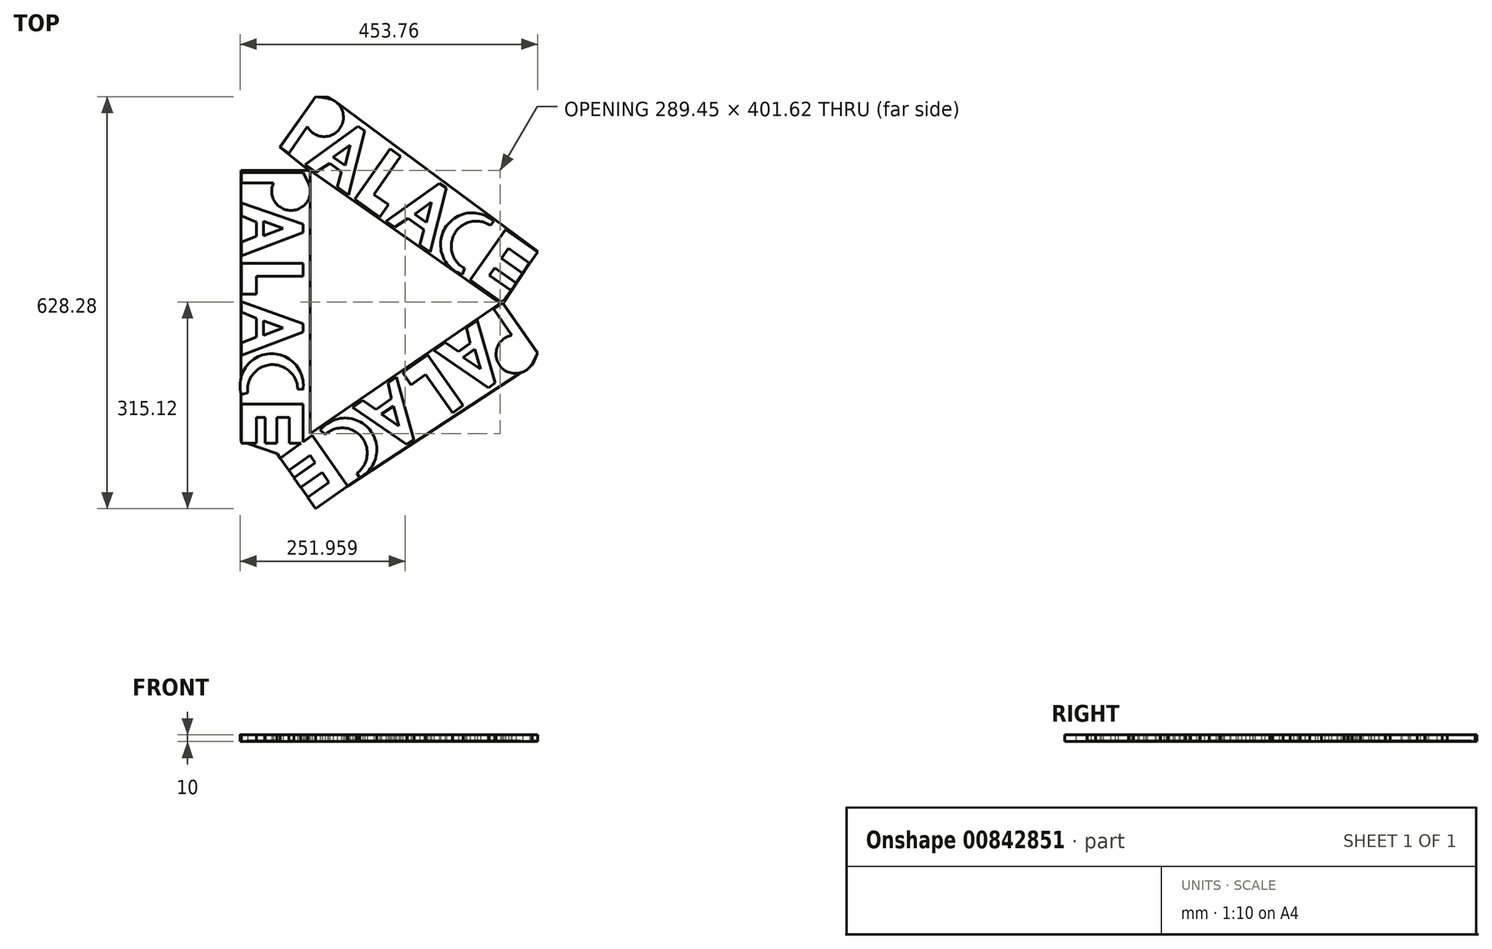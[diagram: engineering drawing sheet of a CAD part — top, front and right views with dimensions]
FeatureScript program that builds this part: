
annotation { "Feature Type Name" : "Feature", "Feature Type Description" : "" }
export const myFeature = defineFeature(function(context is Context, id is Id, definition is map)
    precondition{}
    {
        {
            var Q0;
            Q0=qCreatedBy(makeId("Top.planeOp"),FACE);
            var sketch = newSketch(context, id + "F0", { "sketchPlane" : qUnion([Q0])});
            skLineSegment(sketch, "E0", {"start": v(-235.7, 282.24) * mm, "end": v(-329.78, 282.24) * mm});
            skLineSegment(sketch, "E1", {"start": v(-329.78, 282.24) * mm, "end": v(-329.78, 265.88) * mm});
            skLineSegment(sketch, "E2", {"start": v(-329.78, 265.88) * mm, "end": v(-280.65, 265.88) * mm});
            skLineSegment(sketch, "E3", {"start": v(-329.78, 235.57) * mm, "end": v(-235.7, 203.16) * mm});
            skLineSegment(sketch, "E4", {"start": v(-235.7, 203.16) * mm, "end": v(-235.7, 190.61) * mm});
            skLineSegment(sketch, "E5", {"start": v(-235.7, 190.61) * mm, "end": v(-329.78, 155.07) * mm});
            skLineSegment(sketch, "E6", {"start": v(-329.78, 155.07) * mm, "end": v(-329.78, 175.98) * mm});
            skLineSegment(sketch, "E7", {"start": v(-329.78, 175.98) * mm, "end": v(-307.02, 184.58) * mm});
            skLineSegment(sketch, "E8", {"start": v(-307.02, 184.58) * mm, "end": v(-307.02, 206.3) * mm});
            skLineSegment(sketch, "E9", {"start": v(-307.02, 206.3) * mm, "end": v(-329.78, 215.7) * mm});
            skLineSegment(sketch, "E10", {"start": v(-329.78, 215.7) * mm, "end": v(-329.78, 235.57) * mm});
            skLineSegment(sketch, "E11", {"start": v(-235.7, 143.57) * mm, "end": v(-329.78, 143.57) * mm});
            skLineSegment(sketch, "E12", {"start": v(-329.78, 143.57) * mm, "end": v(-329.78, 96.53) * mm});
            skLineSegment(sketch, "E13", {"start": v(-329.78, 96.53) * mm, "end": v(-307.02, 96.53) * mm});
            skLineSegment(sketch, "E14", {"start": v(-307.02, 96.53) * mm, "end": v(-307.02, 123.7) * mm});
            skLineSegment(sketch, "E15", {"start": v(-307.02, 123.7) * mm, "end": v(-235.7, 123.7) * mm});
            skLineSegment(sketch, "E16", {"start": v(-235.7, 123.7) * mm, "end": v(-235.7, 143.57) * mm});
            skLineSegment(sketch, "E17", {"start": v(-329.78, 85.03) * mm, "end": v(-235.7, 51.57) * mm});
            skLineSegment(sketch, "E18", {"start": v(-235.7, 51.57) * mm, "end": v(-235.7, 39.03) * mm});
            skLineSegment(sketch, "E19", {"start": v(-235.7, 39.03) * mm, "end": v(-329.78, 3.49) * mm});
            skLineSegment(sketch, "E20", {"start": v(-329.78, 3.49) * mm, "end": v(-329.78, 22.3) * mm});
            skLineSegment(sketch, "E21", {"start": v(-329.78, 22.3) * mm, "end": v(-307.02, 30.9) * mm});
            skLineSegment(sketch, "E22", {"start": v(-307.02, 30.9) * mm, "end": v(-307.02, 59.97) * mm});
            skLineSegment(sketch, "E23", {"start": v(-307.02, 59.97) * mm, "end": v(-329.78, 69.38) * mm});
            skLineSegment(sketch, "E24", {"start": v(-329.78, 69.38) * mm, "end": v(-329.78, 85.03) * mm});
            skLineSegment(sketch, "E25", {"start": v(-329.78, -71.04) * mm, "end": v(-329.78, -131.08) * mm});
            skLineSegment(sketch, "E26", {"start": v(-329.78, -131.08) * mm, "end": v(-307.02, -131.08) * mm});
            skLineSegment(sketch, "E27", {"start": v(-307.02, -131.08) * mm, "end": v(-307.02, -91.23) * mm});
            skLineSegment(sketch, "E28", {"start": v(-307.02, -91.23) * mm, "end": v(-293.4, -91.23) * mm});
            skLineSegment(sketch, "E29", {"start": v(-293.4, -91.23) * mm, "end": v(-293.4, -131.08) * mm});
            skLineSegment(sketch, "E30", {"start": v(-293.4, -131.08) * mm, "end": v(-275.39, -131.08) * mm});
            skLineSegment(sketch, "E31", {"start": v(-275.39, -131.08) * mm, "end": v(-275.39, -91.23) * mm});
            skLineSegment(sketch, "E32", {"start": v(-275.39, -91.23) * mm, "end": v(-256.83, -91.23) * mm});
            skLineSegment(sketch, "E33", {"start": v(-256.83, -91.23) * mm, "end": v(-256.83, -131.08) * mm});
            skLineSegment(sketch, "E34", {"start": v(-256.83, -131.08) * mm, "end": v(-235.7, -131.08) * mm});
            skLineSegment(sketch, "E35", {"start": v(-235.7, -131.08) * mm, "end": v(-235.7, -71.04) * mm});
            skLineSegment(sketch, "E36", {"start": v(-235.7, -71.04) * mm, "end": v(-329.78, -71.04) * mm});
            skArc(sketch, "E37", {"start": v(-280.65, 265.88) * mm, "mid": v(-254, 224.07) * mm, "end": v(-227.35, 265.88) * mm});
            skLineSegment(sketch, "E38", {"start": v(-227.35, 265.88) * mm, "end": v(-235.7, 282.24) * mm});
            skArc(sketch, "E39", {"start": v(-235.7, -49.2) * mm, "mid": v(-287.14, 5.5) * mm, "end": v(-329.78, -56.3) * mm});
            skArc(sketch, "E40", {"start": v(-243.73, -48.46) * mm, "mid": v(-284.93, -11.12) * mm, "end": v(-320, -54.26) * mm});
            skLineSegment(sketch, "E41", {"start": v(-243.73, -48.46) * mm, "end": v(-235.7, -49.2) * mm});
            skLineSegment(sketch, "E42", {"start": v(-320, -54.26) * mm, "end": v(-329.78, -56.3) * mm});
            skPoint(sketch, "E43.startSnap0", {"position": v(-282.74, 68.3) * mm});
            skLineSegment(sketch, "E44", {"start": v(-295.92, 55.92) * mm, "end": v(-295.92, 33.9) * mm});
            skLineSegment(sketch, "E45", {"start": v(-295.92, 33.9) * mm, "end": v(-265.9, 45.24) * mm});
            skLineSegment(sketch, "E46", {"start": v(-265.9, 45.24) * mm, "end": v(-295.92, 55.92) * mm});
            skLineSegment(sketch, "E47", {"start": v(-295.84, 207.46) * mm, "end": v(-295.84, 185.44) * mm});
            skLineSegment(sketch, "E48", {"start": v(-295.84, 185.44) * mm, "end": v(-265.81, 196.78) * mm});
            skLineSegment(sketch, "E49", {"start": v(-265.81, 196.78) * mm, "end": v(-295.84, 207.46) * mm});
            skLineSegment(sketch, "E50", {"start": v(122, 6.5) * mm, "end": v(69.17, 81.95) * mm});
            skLineSegment(sketch, "E51", {"start": v(67.01, 82.87) * mm, "end": v(54.63, 74.2) * mm});
            skLineSegment(sketch, "E52", {"start": v(54.63, 74.2) * mm, "end": v(82.81, 33.95) * mm});
            skLineSegment(sketch, "E53", {"start": v(29.8, 56.8) * mm, "end": v(57.22, -38.85) * mm});
            skLineSegment(sketch, "E54", {"start": v(57.22, -38.85) * mm, "end": v(46.94, -46.04) * mm});
            skLineSegment(sketch, "E55", {"start": v(46.94, -46.04) * mm, "end": v(-36.14, 10.64) * mm});
            skLineSegment(sketch, "E56", {"start": v(-36.14, 10.64) * mm, "end": v(-19.01, 22.63) * mm});
            skLineSegment(sketch, "E57", {"start": v(-19.01, 22.63) * mm, "end": v(1.1, 8.91) * mm});
            skLineSegment(sketch, "E58", {"start": v(1.1, 8.91) * mm, "end": v(18.88, 21.37) * mm});
            skLineSegment(sketch, "E59", {"start": v(18.88, 21.37) * mm, "end": v(13.53, 45.42) * mm});
            skLineSegment(sketch, "E60", {"start": v(13.53, 45.42) * mm, "end": v(29.8, 56.8) * mm});
            skLineSegment(sketch, "E61", {"start": v(8.4, -73.03) * mm, "end": v(-45.56, 4.04) * mm});
            skLineSegment(sketch, "E62", {"start": v(-45.56, 4.04) * mm, "end": v(-84.1, -22.94) * mm});
            skLineSegment(sketch, "E63", {"start": v(-84.1, -22.94) * mm, "end": v(-71.04, -41.6) * mm});
            skLineSegment(sketch, "E64", {"start": v(-71.04, -41.6) * mm, "end": v(-48.77, -26) * mm});
            skLineSegment(sketch, "E65", {"start": v(-48.77, -26) * mm, "end": v(-7.87, -84.42) * mm});
            skLineSegment(sketch, "E66", {"start": v(-7.87, -84.42) * mm, "end": v(8.4, -73.03) * mm});
            skLineSegment(sketch, "E67", {"start": v(-93.52, -29.54) * mm, "end": v(-66.95, -125.8) * mm});
            skLineSegment(sketch, "E68", {"start": v(-66.95, -125.8) * mm, "end": v(-77.23, -132.99) * mm});
            skLineSegment(sketch, "E69", {"start": v(-77.23, -132.99) * mm, "end": v(-160.31, -76.3) * mm});
            skLineSegment(sketch, "E70", {"start": v(-160.31, -76.3) * mm, "end": v(-144.9, -65.51) * mm});
            skLineSegment(sketch, "E71", {"start": v(-144.9, -65.51) * mm, "end": v(-124.8, -79.23) * mm});
            skLineSegment(sketch, "E72", {"start": v(-124.8, -79.23) * mm, "end": v(-100.98, -62.56) * mm});
            skLineSegment(sketch, "E73", {"start": v(-100.98, -62.56) * mm, "end": v(-106.34, -38.51) * mm});
            skLineSegment(sketch, "E74", {"start": v(-106.34, -38.51) * mm, "end": v(-93.52, -29.54) * mm});
            skLineSegment(sketch, "E75", {"start": v(-221.36, -119.05) * mm, "end": v(-270.54, -153.49) * mm});
            skLineSegment(sketch, "E76", {"start": v(-270.54, -153.49) * mm, "end": v(-257.48, -172.14) * mm});
            skLineSegment(sketch, "E77", {"start": v(-257.48, -172.14) * mm, "end": v(-224.84, -149.29) * mm});
            skLineSegment(sketch, "E78", {"start": v(-224.84, -149.29) * mm, "end": v(-217.03, -160.44) * mm});
            skLineSegment(sketch, "E79", {"start": v(-217.03, -160.44) * mm, "end": v(-249.67, -183.3) * mm});
            skLineSegment(sketch, "E80", {"start": v(-249.67, -183.3) * mm, "end": v(-239.34, -198.05) * mm});
            skLineSegment(sketch, "E81", {"start": v(-239.34, -198.05) * mm, "end": v(-206.7, -175.2) * mm});
            skLineSegment(sketch, "E82", {"start": v(-206.7, -175.2) * mm, "end": v(-196.05, -190.4) * mm});
            skLineSegment(sketch, "E83", {"start": v(-196.05, -190.4) * mm, "end": v(-228.7, -213.25) * mm});
            skLineSegment(sketch, "E84", {"start": v(-228.7, -213.25) * mm, "end": v(-216.57, -230.56) * mm});
            skLineSegment(sketch, "E85", {"start": v(-216.57, -230.56) * mm, "end": v(-167.4, -196.12) * mm});
            skLineSegment(sketch, "E86", {"start": v(-167.4, -196.12) * mm, "end": v(-221.36, -119.05) * mm});
            skArc(sketch, "E87", {"start": v(82.81, 33.95) * mm, "mid": v(63.85, -11.86) * mm, "end": v(113.39, -9.7) * mm});
            skLineSegment(sketch, "E88", {"start": v(113.39, -9.7) * mm, "end": v(122, 6.5) * mm});
            skArc(sketch, "E89", {"start": v(-149.5, -183.6) * mm, "mid": v(-134.2, -110.08) * mm, "end": v(-209.28, -110.6) * mm});
            skArc(sketch, "E90", {"start": v(-153.5, -176.6) * mm, "mid": v(-146.55, -121.43) * mm, "end": v(-202, -117.44) * mm});
            skLineSegment(sketch, "E91", {"start": v(-153.5, -176.6) * mm, "end": v(-149.5, -183.6) * mm});
            skLineSegment(sketch, "E92", {"start": v(-202, -117.44) * mm, "end": v(-209.28, -110.6) * mm});
            skPoint(sketch, "E93.startSnap0", {"position": v(-80.23, -77.66) * mm});
            skLineSegment(sketch, "E94", {"start": v(-97.93, -73.98) * mm, "end": v(-115.97, -86.6) * mm});
            skLineSegment(sketch, "E95", {"start": v(-115.97, -86.6) * mm, "end": v(-89.46, -104.7) * mm});
            skLineSegment(sketch, "E96", {"start": v(-89.46, -104.7) * mm, "end": v(-97.93, -73.98) * mm});
            skLineSegment(sketch, "E97", {"start": v(26.25, 12.88) * mm, "end": v(8.2, 0.25) * mm});
            skLineSegment(sketch, "E98", {"start": v(8.2, 0.25) * mm, "end": v(34.72, -17.84) * mm});
            skLineSegment(sketch, "E99", {"start": v(34.72, -17.84) * mm, "end": v(26.25, 12.88) * mm});
            skLineSegment(sketch, "E100.0", {"start": v(82.81, 33.95) * mm, "end": v(113.39, -9.7) * mm, "construction": true});
            skLineSegment(sketch, "E101.0", {"start": v(-270.54, -153.49) * mm, "end": v(-228.7, -213.25) * mm, "construction": true});
            skLineSegment(sketch, "E102.0", {"start": v(-221.36, -119.05) * mm, "end": v(-167.4, -196.12) * mm, "construction": true});
            skLineSegment(sketch, "E103.0", {"start": v(-217.03, -160.44) * mm, "end": v(-206.7, -175.2) * mm, "construction": true});
            skLineSegment(sketch, "E104.0", {"start": v(-221.36, -119.05) * mm, "end": v(67.01, 82.87) * mm, "construction": true});
            skLineSegment(sketch, "E105.0", {"start": v(-167.4, -196.12) * mm, "end": v(-77.23, -132.99) * mm, "construction": true});
            skLineSegment(sketch, "E106.0", {"start": v(-257.48, -172.14) * mm, "end": v(1.1, 8.91) * mm, "construction": true});
            skLineSegment(sketch, "E107.0", {"start": v(-7.87, -84.42) * mm, "end": v(122, 6.5) * mm, "construction": true});
            skLineSegment(sketch, "E108.0", {"start": v(29.8, 56.8) * mm, "end": v(54.63, 74.2) * mm, "construction": true});
            skLineSegment(sketch, "E109.0", {"start": v(-66.95, -125.8) * mm, "end": v(8.4, -73.03) * mm, "construction": true});
            skLineSegment(sketch, "E110", {"start": v(-216.57, 397.72) * mm, "end": v(-270.54, 320.65) * mm});
            skLineSegment(sketch, "E111", {"start": v(-270.54, 320.65) * mm, "end": v(-257.14, 311.27) * mm});
            skLineSegment(sketch, "E112", {"start": v(-257.14, 311.27) * mm, "end": v(-228.96, 351.52) * mm});
            skLineSegment(sketch, "E113", {"start": v(-232.3, 293.88) * mm, "end": v(-151.8, 352.36) * mm});
            skLineSegment(sketch, "E114", {"start": v(-151.8, 352.36) * mm, "end": v(-141.52, 345.17) * mm});
            skLineSegment(sketch, "E115", {"start": v(-141.52, 345.17) * mm, "end": v(-166.37, 247.7) * mm});
            skLineSegment(sketch, "E116", {"start": v(-166.37, 247.7) * mm, "end": v(-183.5, 259.7) * mm});
            skLineSegment(sketch, "E117", {"start": v(-183.5, 259.7) * mm, "end": v(-177.48, 283.29) * mm});
            skLineSegment(sketch, "E118", {"start": v(-177.48, 283.29) * mm, "end": v(-195.27, 295.74) * mm});
            skLineSegment(sketch, "E119", {"start": v(-195.27, 295.74) * mm, "end": v(-216.04, 282.49) * mm});
            skLineSegment(sketch, "E120", {"start": v(-216.04, 282.49) * mm, "end": v(-232.3, 293.88) * mm});
            skLineSegment(sketch, "E121", {"start": v(-102.98, 318.18) * mm, "end": v(-156.95, 241.11) * mm});
            skLineSegment(sketch, "E122", {"start": v(-156.95, 241.11) * mm, "end": v(-118.41, 214.13) * mm});
            skLineSegment(sketch, "E123", {"start": v(-118.41, 214.13) * mm, "end": v(-105.35, 232.78) * mm});
            skLineSegment(sketch, "E124", {"start": v(-105.35, 232.78) * mm, "end": v(-127.62, 248.37) * mm});
            skLineSegment(sketch, "E125", {"start": v(-127.62, 248.37) * mm, "end": v(-86.71, 306.8) * mm});
            skLineSegment(sketch, "E126", {"start": v(-86.71, 306.8) * mm, "end": v(-102.98, 318.18) * mm});
            skLineSegment(sketch, "E127", {"start": v(-109, 207.53) * mm, "end": v(-27.63, 265.42) * mm});
            skLineSegment(sketch, "E128", {"start": v(-27.63, 265.42) * mm, "end": v(-17.35, 258.22) * mm});
            skLineSegment(sketch, "E129", {"start": v(-17.35, 258.22) * mm, "end": v(-42.2, 160.76) * mm});
            skLineSegment(sketch, "E130", {"start": v(-42.2, 160.76) * mm, "end": v(-57.61, 171.56) * mm});
            skLineSegment(sketch, "E131", {"start": v(-57.61, 171.56) * mm, "end": v(-51.6, 195.14) * mm});
            skLineSegment(sketch, "E132", {"start": v(-51.6, 195.14) * mm, "end": v(-75.4, 211.81) * mm});
            skLineSegment(sketch, "E133", {"start": v(-75.4, 211.81) * mm, "end": v(-96.17, 198.56) * mm});
            skLineSegment(sketch, "E134", {"start": v(-96.17, 198.56) * mm, "end": v(-109, 207.53) * mm});
            skLineSegment(sketch, "E135", {"start": v(18.85, 118.02) * mm, "end": v(65.66, 85.24) * mm});
            skLineSegment(sketch, "E136", {"start": v(70, 86.4) * mm, "end": v(81.09, 102.23) * mm});
            skLineSegment(sketch, "E137", {"start": v(81.09, 102.23) * mm, "end": v(48.45, 125.09) * mm});
            skLineSegment(sketch, "E138", {"start": v(48.45, 125.09) * mm, "end": v(56.26, 136.24) * mm});
            skLineSegment(sketch, "E139", {"start": v(56.26, 136.24) * mm, "end": v(88.9, 113.39) * mm});
            skLineSegment(sketch, "E140", {"start": v(88.9, 113.39) * mm, "end": v(99.23, 128.14) * mm});
            skLineSegment(sketch, "E141", {"start": v(99.23, 128.14) * mm, "end": v(66.6, 151) * mm});
            skLineSegment(sketch, "E142", {"start": v(66.6, 151) * mm, "end": v(77.24, 166.2) * mm});
            skLineSegment(sketch, "E143", {"start": v(77.24, 166.2) * mm, "end": v(109.88, 143.34) * mm});
            skLineSegment(sketch, "E144", {"start": v(109.88, 143.34) * mm, "end": v(122, 160.65) * mm});
            skLineSegment(sketch, "E145", {"start": v(122, 160.65) * mm, "end": v(72.81, 195.1) * mm});
            skLineSegment(sketch, "E146", {"start": v(72.81, 195.1) * mm, "end": v(18.85, 118.02) * mm});
            skArc(sketch, "E147", {"start": v(-228.96, 351.52) * mm, "mid": v(-179.42, 349.36) * mm, "end": v(-198.39, 395.18) * mm});
            skLineSegment(sketch, "E148", {"start": v(-198.39, 395.18) * mm, "end": v(-216.57, 397.72) * mm});
            skArc(sketch, "E149", {"start": v(54.93, 207.61) * mm, "mid": v(-19.39, 196.86) * mm, "end": v(6.77, 126.47) * mm});
            skArc(sketch, "E150", {"start": v(49.7, 201.46) * mm, "mid": v(-4.5, 189.13) * mm, "end": v(10.72, 135.65) * mm});
            skLineSegment(sketch, "E151", {"start": v(49.7, 201.46) * mm, "end": v(54.93, 207.61) * mm});
            skLineSegment(sketch, "E152", {"start": v(10.72, 135.65) * mm, "end": v(6.77, 126.47) * mm});
            skPoint(sketch, "E153.startSnap0", {"position": v(-68.3, 236.48) * mm});
            skLineSegment(sketch, "E154", {"start": v(-65.72, 218.58) * mm, "end": v(-47.69, 205.95) * mm});
            skLineSegment(sketch, "E155", {"start": v(-47.69, 205.95) * mm, "end": v(-39.76, 237.05) * mm});
            skLineSegment(sketch, "E156", {"start": v(-39.76, 237.05) * mm, "end": v(-65.72, 218.58) * mm});
            skLineSegment(sketch, "E157", {"start": v(-189.81, 305.57) * mm, "end": v(-171.78, 292.94) * mm});
            skLineSegment(sketch, "E158", {"start": v(-171.78, 292.94) * mm, "end": v(-163.84, 324.04) * mm});
            skLineSegment(sketch, "E159", {"start": v(-163.84, 324.04) * mm, "end": v(-189.81, 305.57) * mm});
            skLineSegment(sketch, "E160.0", {"start": v(-228.96, 351.52) * mm, "end": v(-198.39, 395.18) * mm, "construction": true});
            skLineSegment(sketch, "E161.0", {"start": v(70, 86.4) * mm, "end": v(109.88, 143.34) * mm, "construction": true});
            skLineSegment(sketch, "E162.0", {"start": v(18.85, 118.02) * mm, "end": v(72.81, 195.1) * mm, "construction": true});
            skLineSegment(sketch, "E163.0", {"start": v(56.26, 136.24) * mm, "end": v(66.6, 151) * mm, "construction": true});
            skLineSegment(sketch, "E164.0", {"start": v(72.81, 195.1) * mm, "end": v(-17.35, 258.22) * mm, "construction": true});
            skLineSegment(sketch, "E165.0", {"start": v(18.85, 118.02) * mm, "end": v(-270.54, 320.65) * mm, "construction": true});
            skLineSegment(sketch, "E166.0", {"start": v(81.09, 102.23) * mm, "end": v(-177.48, 283.29) * mm, "construction": true});
            skLineSegment(sketch, "E167.0", {"start": v(-232.3, 293.88) * mm, "end": v(-257.14, 311.27) * mm, "construction": true});
            skLineSegment(sketch, "E168.0", {"start": v(-86.71, 306.8) * mm, "end": v(-216.57, 397.72) * mm, "construction": true});
            skLineSegment(sketch, "E169.0", {"start": v(-27.63, 265.42) * mm, "end": v(-102.98, 318.18) * mm, "construction": true});
            skLineSegment(sketch, "E170", {"start": v(70, 86.4) * mm, "end": v(65.66, 85.24) * mm});
            skLineSegment(sketch, "E171", {"start": v(69.17, 81.95) * mm, "end": v(67.01, 82.87) * mm});
            skSolve(sketch);
        }
        {
            var Q0;
            Q0=qCreatedBy(makeId("Top.planeOp"),FACE);
            var sketch = newSketch(context, id + "F1", { "sketchPlane" : qUnion([Q0])});
            skLineSegment(sketch, "E172", {"start": v(-330.45, 285.37) * mm, "end": v(-330.45, -127.9) * mm});
            skLineSegment(sketch, "E173", {"start": v(-217.22, -228.72) * mm, "end": v(99.11, -21.24) * mm});
            skLineSegment(sketch, "E174", {"start": v(99.11, -21.24) * mm, "end": v(114.45, -11.01) * mm});
            skLineSegment(sketch, "E175", {"start": v(114.45, -11.01) * mm, "end": v(121.76, 7.25) * mm});
            skLineSegment(sketch, "E176", {"start": v(121.76, 7.25) * mm, "end": v(69.12, 82.46) * mm});
            skLineSegment(sketch, "E177", {"start": v(69.12, 82.46) * mm, "end": v(99.11, 127.91) * mm});
            skLineSegment(sketch, "E178", {"start": v(99.11, 127.91) * mm, "end": v(121.76, 162.24) * mm});
            skLineSegment(sketch, "E179", {"start": v(121.76, 162.24) * mm, "end": v(-183.97, 388.32) * mm});
            skLineSegment(sketch, "E180", {"start": v(-183.97, 388.32) * mm, "end": v(-197.18, 397.03) * mm});
            skLineSegment(sketch, "E181", {"start": v(-197.18, 397.03) * mm, "end": v(-216.91, 397.03) * mm});
            skLineSegment(sketch, "E182", {"start": v(-216.91, 397.03) * mm, "end": v(-271.2, 320.62) * mm});
            skLineSegment(sketch, "E183", {"start": v(-224.52, 285.37) * mm, "end": v(-224.52, -116.25) * mm});
            skLineSegment(sketch, "E184", {"start": v(-224.52, -116.25) * mm, "end": v(64.92, 82.46) * mm});
            skLineSegment(sketch, "E185", {"start": v(64.92, 82.46) * mm, "end": v(-224.52, 285.37) * mm});
            skLineSegment(sketch, "E186", {"start": v(-330.45, -127.9) * mm, "end": v(-275.16, -146.58) * mm});
            skLineSegment(sketch, "E187", {"start": v(-275.16, -146.58) * mm, "end": v(-217.22, -228.72) * mm});
            skLineSegment(sketch, "E188", {"start": v(-330.45, 285.37) * mm, "end": v(-226.84, 285.37) * mm});
            skLineSegment(sketch, "E189", {"start": v(-226.84, 285.37) * mm, "end": v(-271.2, 320.62) * mm});
            skSolve(sketch);
        }
        {
            var Q0;
            Q0=makeQuery(id+"F1.imprint","IMPRINT",FACE,{"disambiguationData":[TD([[makeQuery(id+"F1.imprint","IMPRINT",EDGE,{"derivedFrom":sQuery(id+"F1.wireOp",EDGE,"E172")}),1.0]])]});
            extrude(context, id + "F2", {"entities" : qUnion([Q0]), "depth" : 1 * mm, "offsetDistance" : 25 * mm});
        }
        {
            var Q0;
            Q0 = qSketchRegion(id + "F0", true);
            extrude(context, id + "F3", {"entities" : qUnion([Q0]), "operationType" : NewBodyOperationType.ADD, "depth" : 10 * mm, "offsetDistance" : 25 * mm});
        }
    });
